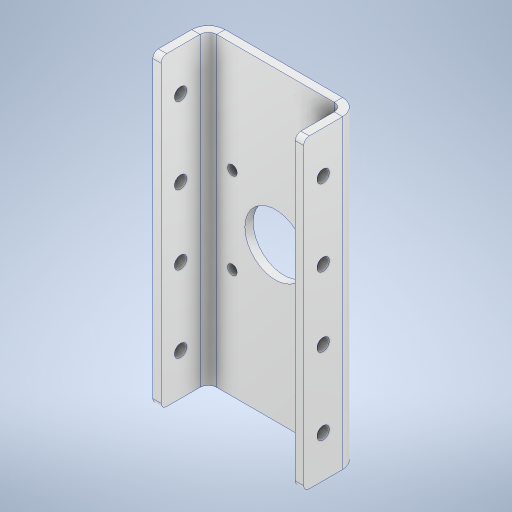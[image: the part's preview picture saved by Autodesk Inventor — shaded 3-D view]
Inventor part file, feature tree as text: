
AUTODESK INVENTOR PART (.ipt)
format: ipt  version: 2024 (Build 280153000, 153)  size: 360,448 bytes
history: native  units: mm
features: other x8, sketch x6, extrude x4, fillet x1
ambient origin geometry x8: Origin, YZ Plane, XZ Plane, XY Plane, X Axis, Y Axis, Z Axis, Center Point
bodies: Volumenkörper1 (feature_tree)
feature tree (19):
  extrude  "Extrusion1"  Depth=42.3mm
  extrude  "Extrusion2"  Depth=3.0mm
  extrude  "Extrusion3"  Depth=15.5mm
  other  "Lasche1"
  other  "Lasche2"
  sketch  "Skizze6"  dims[d14=3.0mm d15=3.0mm d16=1.5mm d17=6.0mm d18=3.0mm d19=20.0mm d20=90.0deg d21=3.0mm d22=12.0mm d23=3.0mm d24=3.0mm d25=3.0mm d26=1.5mm d27=6.0mm d28=3.0mm d29=20.0mm d30=90.0deg d31=3.0mm d32=12.0mm d33=3.0mm d34=3.0mm d35=4.5mm d36=4.5mm d37=25.0mm d40=2.0mm d41=4.5mm d42=4.5mm d43=80.0mm d44=100.0mm d45=0.0mm d46=0.5mm d47=0.872665mm d48=0.5mm d49=0.872665mm]
  fillet  "Rundung2"  Radius=31.0mm
  extrude  "Extrusion5"  Depth=3.5mm
  sketch  "Skizze1"  dims[d0=110.0mm d1=42.3mm]
  sketch  "Skizze2"  dims[d2=3.0mm d3=0.0mm d4=22.0mm]
  sketch  "Skizze3"  dims[d5=4.0mm d6=0.0mm d7=15.5mm d8=31.0mm]
  sketch  "Skizze4"  dims[d9=3.5mm d10=3.5mm]
  other  "Grobblech1"
  other  "Biegung1"
  other  "Ecke1"
  sketch  "Skizze5"  dims[d11=4.0mm d12=0.0mm]
  other  "Grobblech2"
  other  "Biegung2"
  other  "Ecke2"
